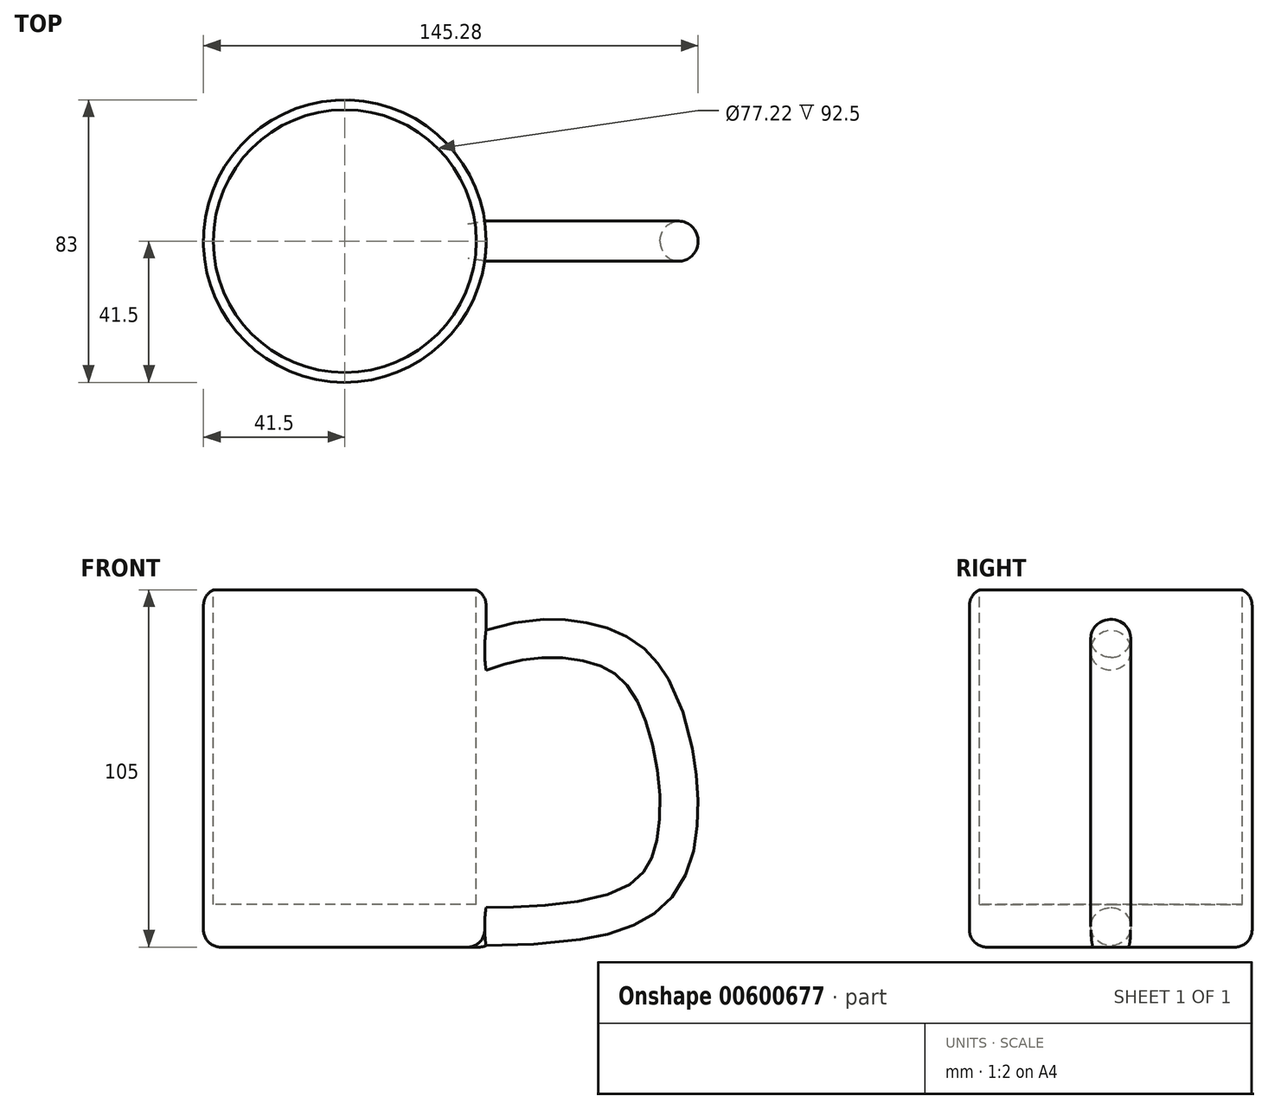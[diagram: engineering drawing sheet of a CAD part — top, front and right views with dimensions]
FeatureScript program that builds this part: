
annotation { "Feature Type Name" : "Feature", "Feature Type Description" : "" }
export const myFeature = defineFeature(function(context is Context, id is Id, definition is map)
    precondition{}
    {
        {
            var Q0;
            Q0=qCreatedBy(makeId("Top.planeOp"),FACE);
            var sketch = newSketch(context, id + "F0", { "sketchPlane" : qUnion([Q0])});
            skCircle(sketch, "E0", {"center": v(0, 0) * mm, "radius": 41.5 * mm});
            skSolve(sketch);
        }
        {
            var Q0;
            Q0 = qSketchRegion(id + "F0", true);
            extrude(context, id + "F1", {"entities" : qUnion([Q0]), "depth" : 105 * mm, "offsetDistance" : 25 * mm});
        }
        {
            var Q0;
            Q0=qCreatedBy(makeId("Right.planeOp"),FACE);
            cPlane(context, id + "F2", {"entities" : qUnion([Q0]), "cplaneType" : CPlaneType.OFFSET, "offset" : 41.5 * mm, "width" : 150 * mm, "height" : 150 * mm});
        }
        {
            var Q0;
            Q0=qCreatedBy(makeId("Front.planeOp"),FACE);
            var sketch = newSketch(context, id + "F3", { "sketchPlane" : qUnion([Q0])});
            skFitSpline(sketch, "E1", {"points": [v(36.07, 86.13) * mm, v(56.56, 91.25) * mm, v(81.8, 86.13) * mm, v(95.2, 65.63) * mm, v(97.95, 30.94) * mm, v(81.8, 10.45) * mm, v(36.07, 5.32) * mm, v(29.37, 5.32) * mm], "startDerivative": vector(146.94, 51.71) * mm, "endDerivative": vector(-63.52, -0.33) * mm});
            skSolve(sketch);
        }
        {
            var Q0;
            Q0=qCreatedBy(id+"F2.planeOp",FACE);
            var sketch = newSketch(context, id + "F4", { "sketchPlane" : qUnion([Q0])});
            skCircle(sketch, "E2", {"center": v(0, 87.26) * mm, "radius": 5.89 * mm});
            skSolve(sketch);
        }
        {
            var Q0;
            Q0 = qSketchRegion(id + "F4", true);
            var Q1;
            Q1 = qConstructionFilter(qBodyType(qCreatedBy(id + "F3" ,EDGE), BodyType.WIRE), ConstructionObject.NO);
            sweep(context, id + "F5", {"operationType" : NewBodyOperationType.ADD, "profiles" : qUnion([Q0]), "path" : qUnion([Q1])});
        }
        {
            var Q0;
            Q0=makeQuery(id+"F1.opExtrude","CAP_FACE",FACE,{"disambiguationData":[OSD([sQuery(id+"F0.wireOp",EDGE,"E0")])],"isStart":false});
            var sketch = newSketch(context, id + "F6", { "sketchPlane" : qUnion([Q0])});
            skCircle(sketch, "E3", {"center": v(0, 0) * mm, "radius": 38.6 * mm});
            skSolve(sketch);
        }
        {
            var Q0;
            Q0 = qSketchRegion(id + "F6", true);
            extrude(context, id + "F7", {"entities" : qUnion([Q0]), "operationType" : NewBodyOperationType.REMOVE, "oppositeDirection" : true, "depth" : 92.5 * mm, "offsetDistance" : 25 * mm});
        }
        {
            var Q0;
            Q0=makeQuery(id+"F1.opExtrude","CAP_EDGE",EDGE,{"disambiguationData":[OSD([sQuery(id+"F0.wireOp",EDGE,"E0")])],"isStart":false});
            var Q1;
            Q1=makeQuery(id+"F1.opExtrude","CAP_EDGE",EDGE,{"disambiguationData":[OSD([sQuery(id+"F0.wireOp",EDGE,"E0")])],"isStart":true});
            fillet(context, id + "F8", {"entities" : qUnion([Q0, Q1]), "radius" : 5 * mm, "tangentPropagation" : true, "allowEdgeOverflow" : false});
        }
    });
